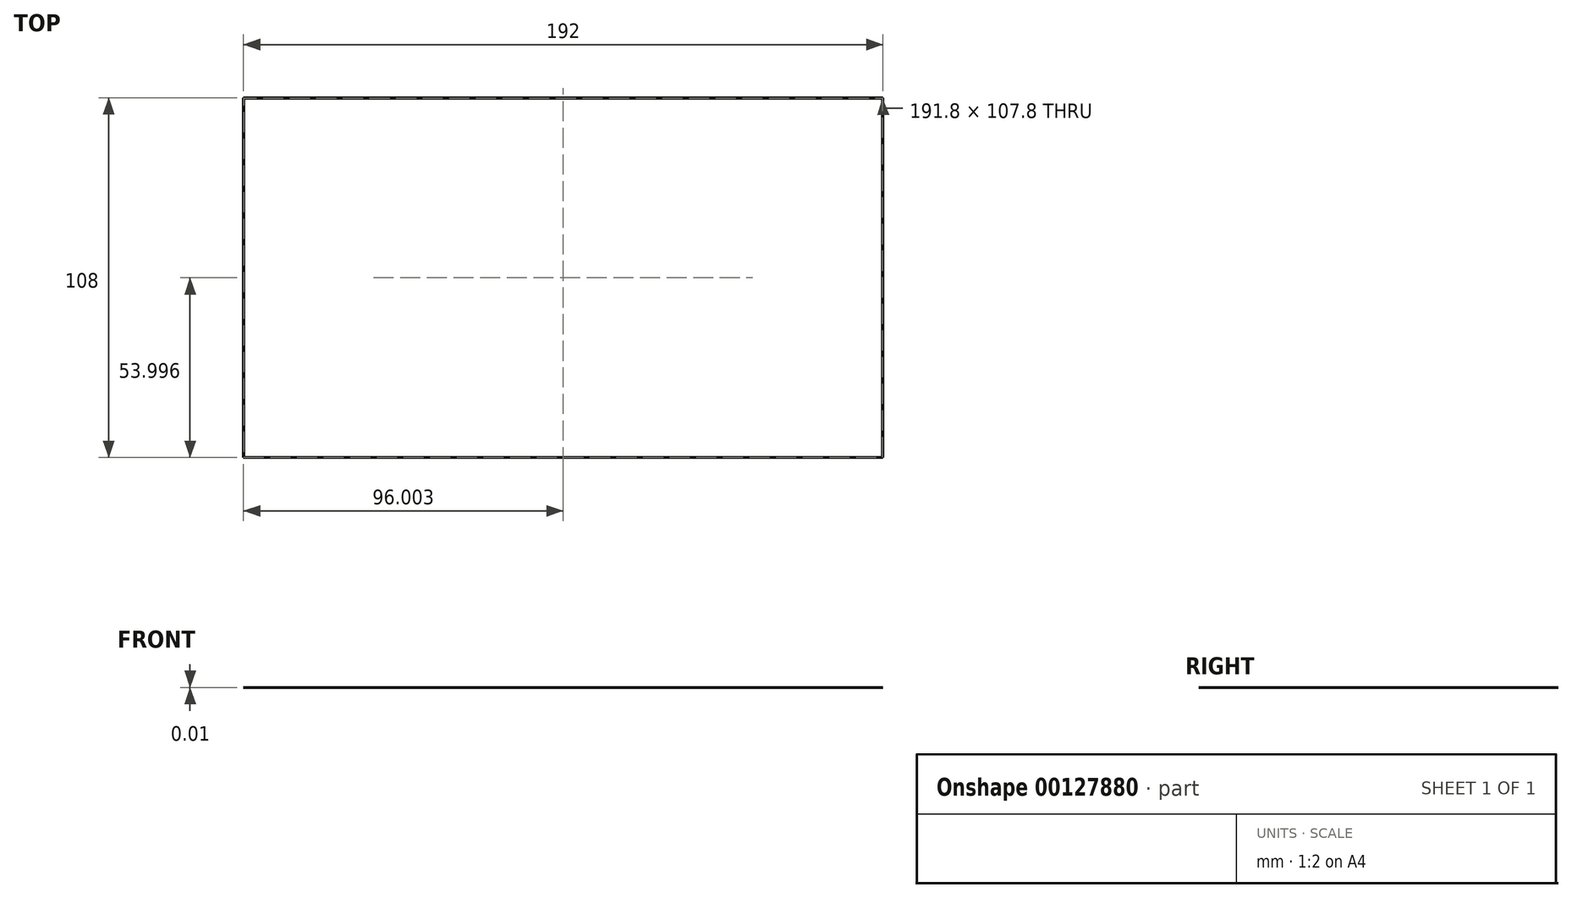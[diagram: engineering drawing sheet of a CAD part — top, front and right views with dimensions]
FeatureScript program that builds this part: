
annotation { "Feature Type Name" : "Feature", "Feature Type Description" : "" }
export const myFeature = defineFeature(function(context is Context, id is Id, definition is map)
    precondition{}
    {
        {
            var Q0;
            Q0=qCreatedBy(makeId("Top.planeOp"),FACE);
            var sketch = newSketch(context, id + "F0", { "sketchPlane" : qUnion([Q0])});
            skLineSegment(sketch, "E0.bottom", {"start": v(-98.36, 55.99) * mm, "end": v(93.64, 55.99) * mm});
            skLineSegment(sketch, "E0.top", {"start": v(-98.36, -52.01) * mm, "end": v(93.64, -52.01) * mm});
            skLineSegment(sketch, "E0.left", {"start": v(-98.36, 55.99) * mm, "end": v(-98.36, -52.01) * mm});
            skLineSegment(sketch, "E0.right", {"start": v(93.64, 55.99) * mm, "end": v(93.64, -52.01) * mm});
            skLineSegment(sketch, "E1.0", {"start": v(-98.26, 55.89) * mm, "end": v(93.54, 55.89) * mm});
            skLineSegment(sketch, "E1.1", {"start": v(-98.26, 55.89) * mm, "end": v(-98.26, -51.91) * mm});
            skLineSegment(sketch, "E1.2", {"start": v(-98.26, -51.91) * mm, "end": v(93.54, -51.91) * mm});
            skLineSegment(sketch, "E1.3", {"start": v(93.54, 55.89) * mm, "end": v(93.54, -51.91) * mm});
            skSolve(sketch);
        }
        {
            var Q0;
            Q0=makeQuery(id+"F0.imprint","IMPRINT",FACE,{"disambiguationData":[TD([[makeQuery(id+"F0.imprint","IMPRINT",EDGE,{"derivedFrom":sQuery(id+"F0.wireOp",EDGE,"E0.bottom")}),-1.0]])]});
            extrude(context, id + "F1", {"entities" : qUnion([Q0]), "depth" : 0.01 * mm});
        }
    });
